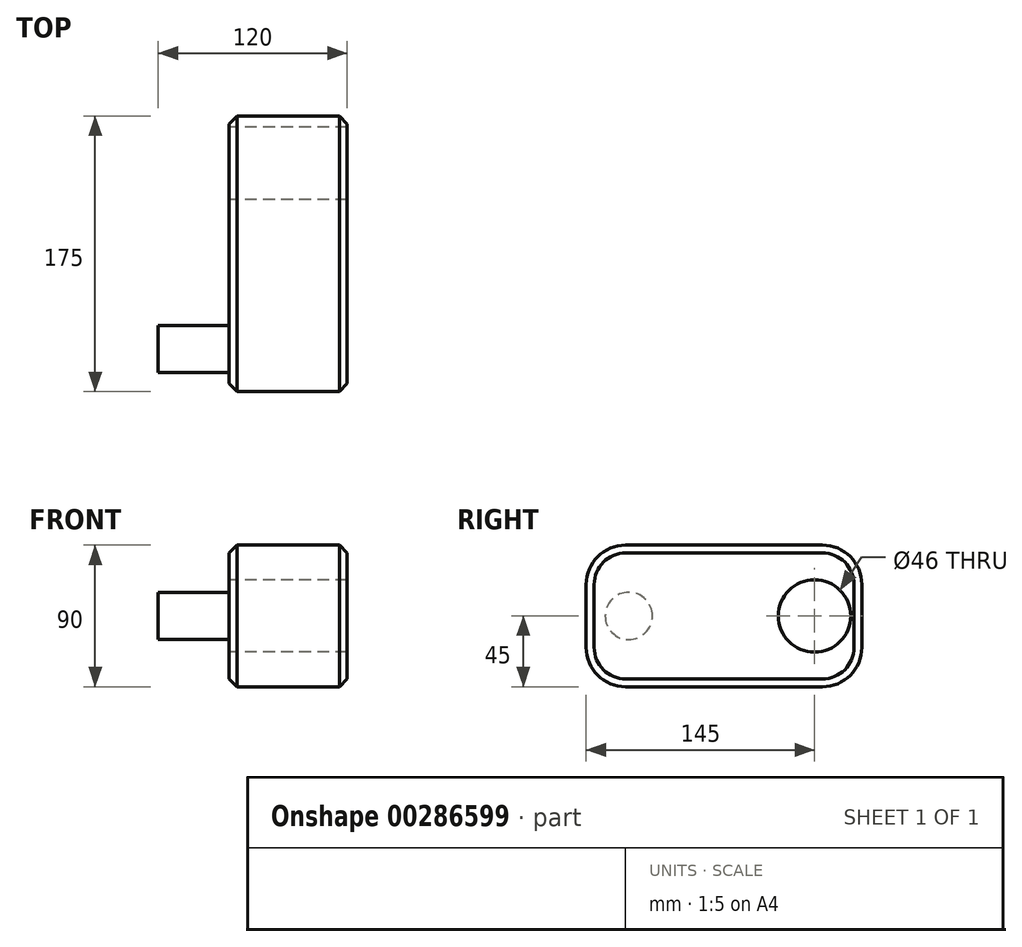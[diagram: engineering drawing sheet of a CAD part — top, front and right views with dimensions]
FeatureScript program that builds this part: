
annotation { "Feature Type Name" : "Feature", "Feature Type Description" : "" }
export const myFeature = defineFeature(function(context is Context, id is Id, definition is map)
    precondition{}
    {
        {
            var Q0;
            Q0=qCreatedBy(makeId("Front.planeOp"),FACE);
            var sketch = newSketch(context, id + "F0", { "sketchPlane" : qUnion([Q0])});
            skLineSegment(sketch, "E0.bottom", {"start": v(-37.5, 45) * mm, "end": v(37.5, 45) * mm});
            skLineSegment(sketch, "E0.top", {"start": v(-37.5, -45) * mm, "end": v(37.5, -45) * mm});
            skLineSegment(sketch, "E0.left", {"start": v(-37.5, 45) * mm, "end": v(-37.5, -45) * mm});
            skLineSegment(sketch, "E0.right", {"start": v(37.5, 45) * mm, "end": v(37.5, -45) * mm});
            skPoint(sketch, "E0.middle", {"position": v(0, 0) * mm});
            skSolve(sketch);
        }
        {
            var Q0;
            Q0=makeQuery(id+"F0.imprint","IMPRINT",FACE,{"disambiguationData":[TD([[makeQuery(id+"F0.imprint","IMPRINT",EDGE,{"derivedFrom":sQuery(id+"F0.wireOp",EDGE,"E0.bottom")}),-1.0]])]});
            extrude(context, id + "F1", {"entities" : qUnion([Q0]), "depth" : 175 * mm});
        }
        {
            var Q0;
            Q0=makeQuery(id+"F1.opExtrude","CAP_EDGE",EDGE,{"disambiguationData":[OSD([sQuery(id+"F0.wireOp",EDGE,"E0.bottom")])],"isStart":true});
            var Q1;
            Q1=makeQuery(id+"F1.opExtrude","CAP_EDGE",EDGE,{"disambiguationData":[OSD([sQuery(id+"F0.wireOp",EDGE,"E0.top")])],"isStart":true});
            var Q2;
            Q2=makeQuery(id+"F1.opExtrude","CAP_EDGE",EDGE,{"disambiguationData":[OSD([sQuery(id+"F0.wireOp",EDGE,"E0.top")])],"isStart":false});
            var Q3;
            Q3=makeQuery(id+"F1.opExtrude","CAP_EDGE",EDGE,{"disambiguationData":[OSD([sQuery(id+"F0.wireOp",EDGE,"E0.bottom")])],"isStart":false});
            fillet(context, id + "F2", {"entities" : qUnion([Q0, Q1, Q2, Q3]), "radius" : 25 * mm, "tangentPropagation" : true, "allowEdgeOverflow" : false});
        }
        {
            var Q0;
            Q0=makeQuery(id+"F1.opExtrude","SWEPT_EDGE",EDGE,{"disambiguationData":[OSD([sQuery(id+"F0.wireOp",EDGE,"E0.bottom"),sQuery(id+"F0.wireOp",EDGE,"E0.left")])]});
            var Q1;
            Q1=makeQuery(id+"F2.opFillet","BLEND_EDGE",EDGE,{"blendedFrom":[makeQuery(id+"F1.opExtrude","CAP_EDGE",EDGE,{"disambiguationData":[OSD([sQuery(id+"F0.wireOp",EDGE,"E0.bottom")])],"isStart":false}),makeQuery(id+"F1.opExtrude","SWEPT_FACE",FACE,{"disambiguationData":[OSD([sQuery(id+"F0.wireOp",EDGE,"E0.right")])]})],"blendedInto":[makeQuery(id+"F1.opExtrude","SWEPT_FACE",FACE,{"disambiguationData":[OSD([sQuery(id+"F0.wireOp",EDGE,"E0.right")])]})]});
            chamfer(context, id + "F3", {"entities" : qUnion([Q0, Q1]), "width" : 5 * mm, "tangentPropagation" : true});
        }
        {
            var Q0;
            Q0=makeQuery(id+"F1.opExtrude","SWEPT_FACE",FACE,{"disambiguationData":[OSD([sQuery(id+"F0.wireOp",EDGE,"E0.left")])]});
            var sketch = newSketch(context, id + "F4", { "sketchPlane" : qUnion([Q0])});
            skCircle(sketch, "E1", {"center": v(30, 0) * mm, "radius": 23 * mm});
            skSolve(sketch);
        }
        {
            var Q0;
            Q0=makeQuery(id+"F4.imprint","IMPRINT",FACE,{"disambiguationData":[TD([[makeQuery(id+"F4.imprint","IMPRINT",EDGE,{"derivedFrom":sQuery(id+"F4.wireOp",EDGE,"E1")}),1.0]])]});
            extrude(context, id + "F5", {"entities" : qUnion([Q0]), "operationType" : NewBodyOperationType.REMOVE, "endBound" : BoundingType.THROUGH_ALL, "oppositeDirection" : true, "depth" : 25 * mm});
        }
        {
            var Q0;
            Q0=makeQuery(id+"F1.opExtrude","SWEPT_FACE",FACE,{"disambiguationData":[OSD([sQuery(id+"F0.wireOp",EDGE,"E0.left")])]});
            var sketch = newSketch(context, id + "F6", { "sketchPlane" : qUnion([Q0])});
            skCircle(sketch, "E2", {"center": v(148, 0) * mm, "radius": 15 * mm});
            skSolve(sketch);
        }
        {
            var Q0;
            Q0=makeQuery(id+"F6.imprint","IMPRINT",FACE,{"disambiguationData":[TD([[makeQuery(id+"F6.imprint","IMPRINT",EDGE,{"derivedFrom":sQuery(id+"F6.wireOp",EDGE,"E2")}),1.0]])]});
            extrude(context, id + "F7", {"entities" : qUnion([Q0]), "operationType" : NewBodyOperationType.ADD, "depth" : 45 * mm});
        }
    });
